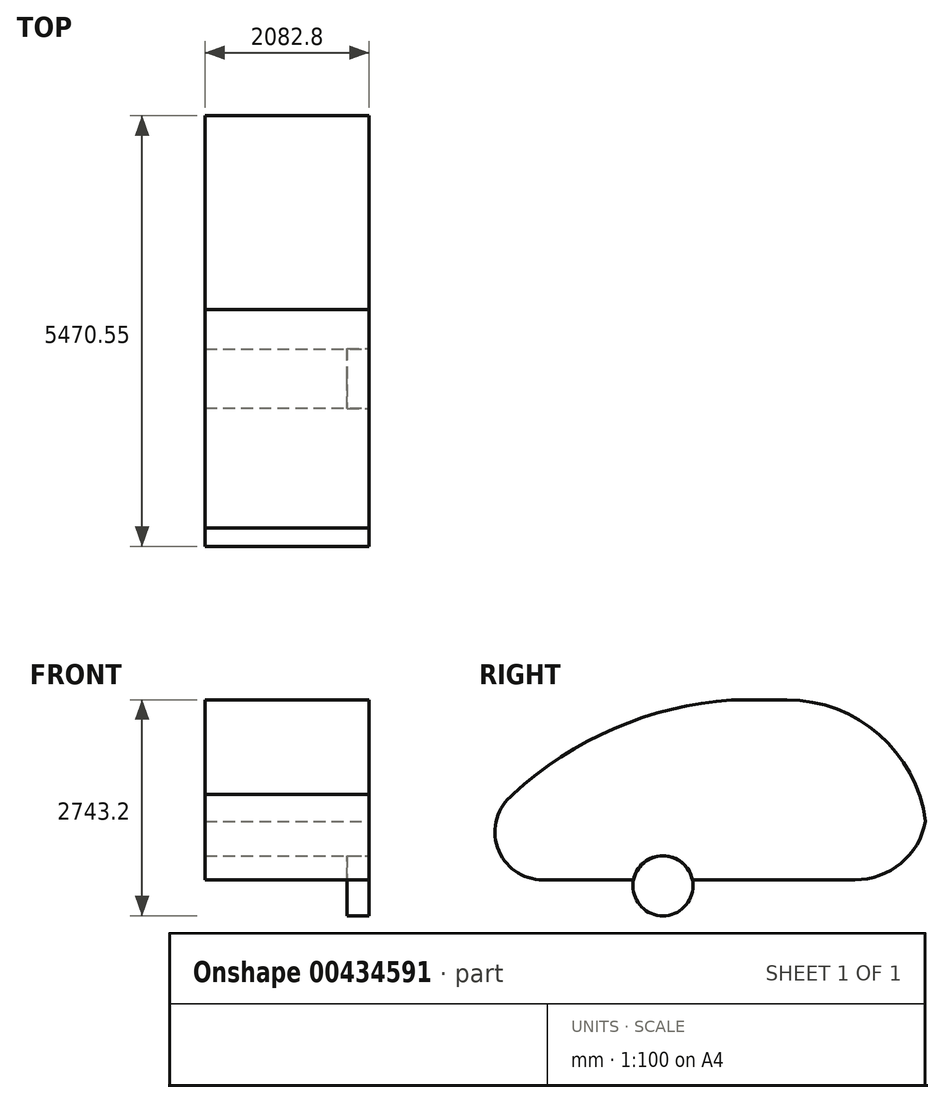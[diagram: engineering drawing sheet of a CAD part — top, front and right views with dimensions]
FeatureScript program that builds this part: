
annotation { "Feature Type Name" : "Feature", "Feature Type Description" : "" }
export const myFeature = defineFeature(function(context is Context, id is Id, definition is map)
    precondition{}
    {
        {
            var Q0;
            Q0=qCreatedBy(makeId("Right.planeOp"),FACE);
            var sketch = newSketch(context, id + "F0", { "sketchPlane" : qUnion([Q0])});
            skLineSegment(sketch, "E0", {"start": v(0, 0) * mm, "end": v(5486.4, 0) * mm, "construction": true});
            skLineSegment(sketch, "E1", {"start": v(5486.4, 0) * mm, "end": v(5486.4, 2743.2) * mm, "construction": true});
            skLineSegment(sketch, "E2", {"start": v(3708.4, 2743.2) * mm, "end": v(3005.32, 2743.2) * mm});
            skLineSegment(sketch, "E3", {"start": v(0, 2743.2) * mm, "end": v(0, 0) * mm, "construction": true});
            skCircle(sketch, "E4", {"center": v(2133.6, 381) * mm, "radius": 381 * mm});
            skLineSegment(sketch, "E5", {"start": v(609.6, 457.2) * mm, "end": v(5486.4, 457.2) * mm});
            skArc(sketch, "E6", {"start": v(231.15, 1544.7) * mm, "mid": v(33.86, 866.45) * mm, "end": v(609.6, 457.2) * mm});
            skArc(sketch, "E7", {"start": v(5470.55, 1202.08) * mm, "mid": v(4878.9, 2303.57) * mm, "end": v(3708.4, 2743.2) * mm});
            skArc(sketch, "E8", {"start": v(4572, 457.2) * mm, "mid": v(5155.58, 667.63) * mm, "end": v(5470.55, 1202.08) * mm});
            skArc(sketch, "E9.trimOffspring", {"start": v(3005.32, 2743.2) * mm, "mid": v(1516.35, 2379.78) * mm, "end": v(231.15, 1544.7) * mm});
            skLineSegment(sketch, "E10", {"start": v(-1611.25, 2590.8) * mm, "end": v(7473.73, 2590.8) * mm, "construction": true});
            skSolve(sketch);
        }
        {
            var Q0;
            Q0=makeQuery(id+"F0.imprint","IMPRINT",FACE,{"disambiguationData":[TD([[makeQuery(id+"F0.imprint","IMPRINT",EDGE,{"derivedFrom":sQuery(id+"F0.wireOp",EDGE,"E2")}),1.0]])]});
            extrude(context, id + "F1", {"entities" : qUnion([Q0]), "oppositeDirection" : true, "depth" : 2082.8 * mm});
        }
        {
            var Q0;
            {var subQ0=sQuery(id+"F0.wireOp",EDGE,"E5");var subQ1=sQuery(id+"F0.wireOp",EDGE,"E4");var subQ2=makeQuery(id+"F0.imprint","INTERSECT",VERTEX,{"disambiguationData":[OD(0.0)],"derivedFrom":[subQ1,subQ0]});Q0=makeQuery(id+"F0.imprint","IMPRINT",FACE,{"disambiguationData":[TD([[makeQuery(id+"F0.imprint","IMPRINT",EDGE,{"disambiguationData":[TD([[subQ2,1.0]])],"derivedFrom":subQ1}),1.0]])]});}
            var Q1;
            {var subQ0=sQuery(id+"F0.wireOp",EDGE,"E5");var subQ1=sQuery(id+"F0.wireOp",EDGE,"E4");var subQ2=makeQuery(id+"F0.imprint","INTERSECT",VERTEX,{"disambiguationData":[OD(0.0)],"derivedFrom":[subQ1,subQ0]});Q1=makeQuery(id+"F0.imprint","IMPRINT",FACE,{"disambiguationData":[TD([[makeQuery(id+"F0.imprint","IMPRINT",EDGE,{"disambiguationData":[TD([[subQ2,-1.0]])],"derivedFrom":subQ1}),1.0]])]});}
            extrude(context, id + "F2", {"entities" : qUnion([Q0, Q1]), "oppositeDirection" : true, "depth" : 279.4 * mm});
        }
    });
